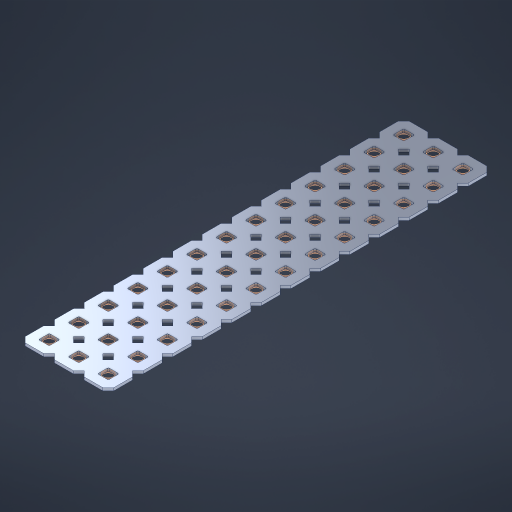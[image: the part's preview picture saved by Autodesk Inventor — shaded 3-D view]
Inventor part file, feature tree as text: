
AUTODESK INVENTOR PART (.ipt)
format: ipt  version: 2023 (Build 270158000, 158)  size: 708,608 bytes
history: native  units: in
note: dims shown in document units (in); Inventor stores cm internally (conversion verified against a paired STEP export)
features: other x40, extrude x38, sketch x2, pattern_linear x1
ambient origin geometry x8: Origin, YZ Plane, XZ Plane, XY Plane, X Axis, Y Axis, Z Axis, Center Point
bodies: Solid1 (feature_tree), Body (feature_tree)
feature tree (81):
  pattern_linear  "Rectangular Pattern1"  Spacing1=0.09in  [1 undecoded]
  sketch  "Sketch1"  dims[d1=0.5in]
  sketch  "Sketch2"  dims[d2=0.182in d3=0.09in d4=0.09in d5=0.09in d6=0.09in d7=0.09in d8=0.09in d9=0.09in d10=0.09in d11=0.02in d13=0.0in d14=0.172in d15=0.0625in d16=0.0in d19=0.5in d22=0.5in]
  other  "Srf1"
  other  "Srf126"
  other  "Srf127"
  other  "Srf128"
  other  "Srf129"
  other  "Srf130"
  other  "Srf131"
  other  "Srf250"
  other  "Srf251"
  other  "Srf252"
  other  "Srf253"
  other  "Srf254"
  other  "Srf255"
  other  "Srf268"
  other  "Srf269"
  other  "Srf270"
  other  "Srf271"
  other  "Srf272"
  other  "Srf273"
  other  "Srf274"
  other  "Srf275"
  other  "Srf276"
  other  "Srf277"
  other  "Srf278"
  other  "Srf279"
  other  "Srf280"
  other  "Srf293"
  other  "Srf294"
  other  "Srf295"
  other  "Srf296"
  other  "Srf297"
  other  "Srf298"
  other  "Srf299"
  other  "Srf300"
  other  "Srf301"
  other  "Srf302"
  other  "Srf303"
  other  "Srf304"
  other  "Srf305"
  other  "Circle"
  extrude  "ExtrusionSrf126"  Depth=0.09in
  extrude  "ExtrusionSrf127"  Depth=0.09in
  extrude  "ExtrusionSrf128"  Depth=0.09in
  extrude  "ExtrusionSrf129"  Depth=0.09in
  extrude  "ExtrusionSrf130"  Depth=0.09in
  extrude  "ExtrusionSrf131"  Depth=0.09in
  extrude  "ExtrusionSrf250"  Depth=0.09in
  extrude  "ExtrusionSrf251"  Depth=0.02in
  extrude  "ExtrusionSrf252"  TaperAngle=0.0deg  [1 undecoded]
  extrude  "ExtrusionSrf253"  Depth=0.5in
  extrude  "ExtrusionSrf254"  Depth=0.5in TaperAngle=0.0deg
  extrude  "ExtrusionSrf255"  Depth=0.5in
  extrude  "ExtrusionSrf268"  Depth=0.5in
  extrude  "ExtrusionSrf269"  [1 undecoded]
  extrude  "ExtrusionSrf270"  [1 undecoded]
  extrude  "ExtrusionSrf271"  [1 undecoded]
  extrude  "ExtrusionSrf272"  [1 undecoded]
  extrude  "ExtrusionSrf273"  [1 undecoded]
  extrude  "ExtrusionSrf274"  [1 undecoded]
  extrude  "ExtrusionSrf275"  [1 undecoded]
  extrude  "ExtrusionSrf276"  [1 undecoded]
  extrude  "ExtrusionSrf277"  [1 undecoded]
  extrude  "ExtrusionSrf278"  [1 undecoded]
  extrude  "ExtrusionSrf279"  [1 undecoded]
  extrude  "ExtrusionSrf280"  [1 undecoded]
  extrude  "ExtrusionSrf293"  [1 undecoded]
  extrude  "ExtrusionSrf294"  [1 undecoded]
  extrude  "ExtrusionSrf295"  [1 undecoded]
  extrude  "ExtrusionSrf296"  [1 undecoded]
  extrude  "ExtrusionSrf297"  [1 undecoded]
  extrude  "ExtrusionSrf298"  [1 undecoded]
  extrude  "ExtrusionSrf299"  [1 undecoded]
  extrude  "ExtrusionSrf300"  [1 undecoded]
  extrude  "ExtrusionSrf301"  [1 undecoded]
  extrude  "ExtrusionSrf302"  [1 undecoded]
  extrude  "ExtrusionSrf303"  [1 undecoded]
  extrude  "ExtrusionSrf304"  [1 undecoded]
  extrude  "ExtrusionSrf305"  [1 undecoded]
note: 27 required parameter values undecoded (feature->parameter linkage not recoverable at this tier; creation-order binding heuristic only, values carry confidence <= 0.55)
